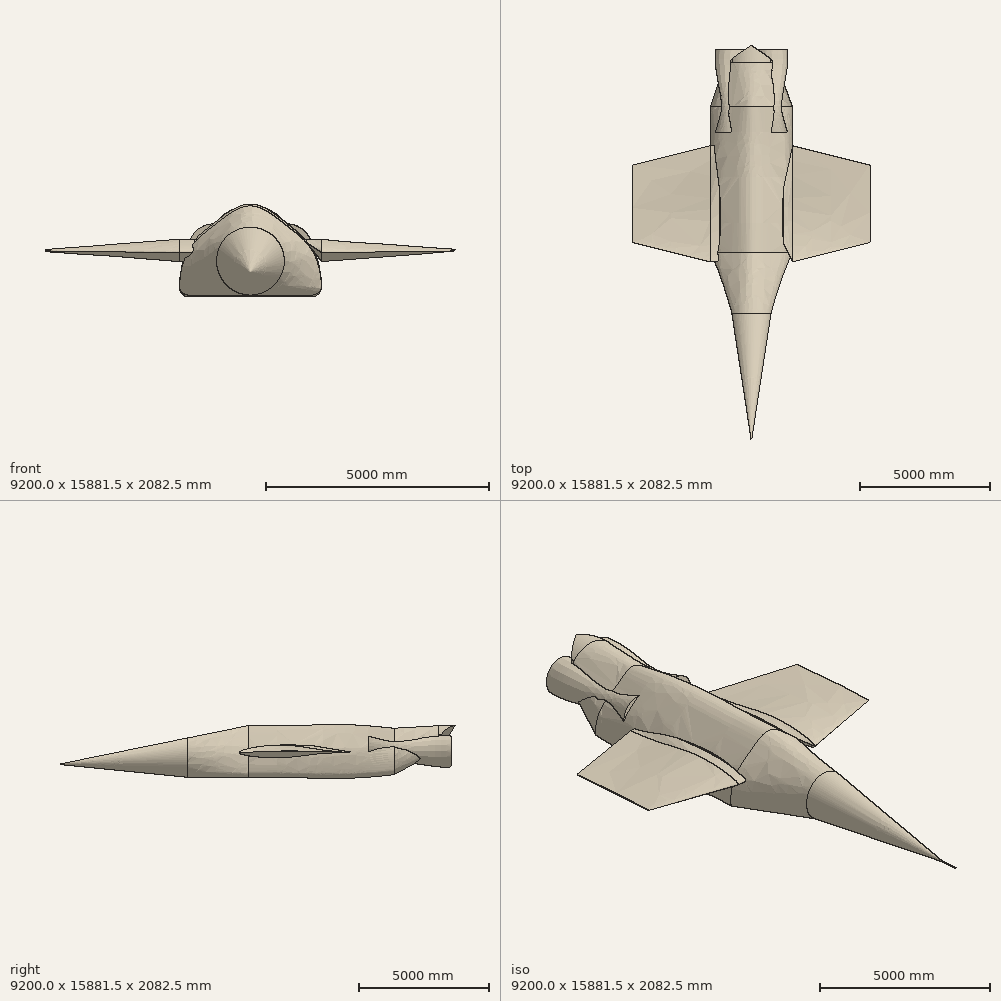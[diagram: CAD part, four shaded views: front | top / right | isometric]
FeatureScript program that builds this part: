
annotation { "Feature Type Name" : "Feature", "Feature Type Description" : "" }
export const myFeature = defineFeature(function(context is Context, id is Id, definition is map)
    precondition{}
    {
        {
            var Q0;
            Q0=qCreatedBy(makeId("Right.planeOp"),FACE);
            var sketch = newSketch(context, id + "F0", { "sketchPlane" : qUnion([Q0])});
            skLineSegment(sketch, "E0", {"start": v(0, 0) * mm, "end": v(-1750, 0) * mm});
            skLineSegment(sketch, "E1", {"start": v(-1750, 0) * mm, "end": v(-3500, 0) * mm});
            skLineSegment(sketch, "E2", {"start": v(-3500, 0) * mm, "end": v(-3500, -1000) * mm});
            skLineSegment(sketch, "E3", {"start": v(-3500, -1000) * mm, "end": v(-8500, -1000) * mm});
            skLineSegment(sketch, "E4", {"start": v(-8500, -1000) * mm, "end": v(-8500, -499.31) * mm});
            skLineSegment(sketch, "E5", {"start": v(-1151.4, 0) * mm, "end": v(-1151.4, 1000) * mm});
            skLineSegment(sketch, "E6", {"start": v(-1151.4, 1000) * mm, "end": v(-8500, -499.31) * mm});
            skLineSegment(sketch, "E7", {"start": v(-8500, -499.31) * mm, "end": v(-3500, -1000) * mm});
            skLineSegment(sketch, "E8", {"start": v(-3500, 0) * mm, "end": v(-3500, 520.82) * mm});
            skLineSegment(sketch, "E9", {"start": v(-8500, -499.31) * mm, "end": v(-8450, -499.31) * mm});
            skLineSegment(sketch, "E10", {"start": v(-8450, -499.31) * mm, "end": v(-8450, -489.1) * mm});
            skLineSegment(sketch, "E11", {"start": v(-8450, -499.31) * mm, "end": v(-8450, -504.32) * mm});
            skSolve(sketch);
        }
        {
            var Q0;
            Q0=sQuery(id+"F0.wireOp",EDGE,"E5");
            cPlane(context, id + "F1", {"entities" : qUnion([Q0]), "cplaneType" : CPlaneType.LINE_ANGLE, "offset" : 25 * mm, "angle" : 90 * degree, "oppositeDirection" : true, "width" : 150 * mm, "height" : 150 * mm});
        }
        {
            var Q0;
            Q0=qCreatedBy(id+"F1.planeOp",FACE);
            var sketch = newSketch(context, id + "F2", { "sketchPlane" : qUnion([Q0])});
            skLineSegment(sketch, "E12.top", {"start": v(-1394.2, -1000) * mm, "end": v(1394.2, -1000) * mm});
            skPoint(sketch, "E12.middle", {"position": v(0, 0) * mm});
            skFitSpline(sketch, "E13", {"points": [v(-1600, -1000) * mm, v(-848, 530) * mm, v(0, 1000) * mm, v(848, 530) * mm, v(1600, -1000) * mm], "startDerivative": vector(0, 10524.75) * mm, "endDerivative": vector(0, -10524.75) * mm});
            skArc(sketch, "E14", {"start": v(-735.27, 618.52) * mm, "mid": v(-1273.27, 435.52) * mm, "end": v(-1440.68, -107.53) * mm});
            skArc(sketch, "E15", {"start": v(1440.68, -107.53) * mm, "mid": v(1273.27, 435.52) * mm, "end": v(735.27, 618.52) * mm});
            skFitSpline(sketch, "E16.trimOffspring", {"points": [v(-1600, -1000) * mm, v(-848, 530) * mm, v(0, 1000) * mm, v(848, 530) * mm, v(1600, -1000) * mm], "startDerivative": vector(0, 10524.75) * mm, "endDerivative": vector(0, -10524.75) * mm});
            skFitSpline(sketch, "E17.trimOffspring", {"points": [v(-1600, -1000) * mm, v(-848, 530) * mm, v(0, 1000) * mm, v(848, 530) * mm, v(1600, -1000) * mm], "startDerivative": vector(0, 10524.75) * mm, "endDerivative": vector(0, -10524.75) * mm});
            skArc(sketch, "E18.filletArc", {"start": v(-1593.82, -787.83) * mm, "mid": v(-1539.85, -937.05) * mm, "end": v(-1394.2, -1000) * mm});
            skArc(sketch, "E19.filletArc", {"start": v(1394.2, -1000) * mm, "mid": v(1539.85, -937.05) * mm, "end": v(1593.82, -787.83) * mm});
            skSolve(sketch);
        }
        {
            var Q0;
            Q0=qCreatedBy(makeId("Front.planeOp"),FACE);
            var sketch = newSketch(context, id + "F3", { "sketchPlane" : qUnion([Q0])});
            skLineSegment(sketch, "E20.top", {"start": v(-1394.2, -1000) * mm, "end": v(1394.2, -1000) * mm});
            skPoint(sketch, "E20.middle", {"position": v(0, 0) * mm});
            skFitSpline(sketch, "E21", {"points": [v(-1600, -1000) * mm, v(-848, 530) * mm, v(0, 1000) * mm, v(848, 530) * mm, v(1600, -1000) * mm], "startDerivative": vector(0, 10524.75) * mm, "endDerivative": vector(0, -10524.75) * mm});
            skArc(sketch, "E22", {"start": v(-735.27, 618.52) * mm, "mid": v(-1273.27, 435.52) * mm, "end": v(-1440.68, -107.53) * mm});
            skArc(sketch, "E23", {"start": v(1440.68, -107.53) * mm, "mid": v(1273.27, 435.52) * mm, "end": v(735.27, 618.52) * mm});
            skFitSpline(sketch, "E24.trimOffspring", {"points": [v(-1600, -1000) * mm, v(-848, 530) * mm, v(0, 1000) * mm, v(848, 530) * mm, v(1600, -1000) * mm], "startDerivative": vector(0, 10524.75) * mm, "endDerivative": vector(0, -10524.75) * mm});
            skFitSpline(sketch, "E25.trimOffspring", {"points": [v(-1600, -1000) * mm, v(-848, 530) * mm, v(0, 1000) * mm, v(848, 530) * mm, v(1600, -1000) * mm], "startDerivative": vector(0, 10524.75) * mm, "endDerivative": vector(0, -10524.75) * mm});
            skArc(sketch, "E26.filletArc", {"start": v(-1593.82, -787.83) * mm, "mid": v(-1539.85, -937.05) * mm, "end": v(-1394.2, -1000) * mm});
            skArc(sketch, "E27.filletArc", {"start": v(1394.2, -1000) * mm, "mid": v(1539.85, -937.05) * mm, "end": v(1593.82, -787.83) * mm});
            skSolve(sketch);
        }
        {
            var Q0;
            Q0=qCreatedBy(makeId("Front.planeOp"),FACE);
            cPlane(context, id + "F4", {"entities" : qUnion([Q0]), "cplaneType" : CPlaneType.OFFSET, "offset" : 3500 * mm, "oppositeDirection" : true, "width" : 150 * mm, "height" : 150 * mm});
        }
        {
            var Q0;
            Q0=qCreatedBy(id+"F4.planeOp",FACE);
            var sketch = newSketch(context, id + "F5", { "sketchPlane" : qUnion([Q0])});
            skLineSegment(sketch, "E28.top", {"start": v(-1394.2, -1000) * mm, "end": v(1394.2, -1000) * mm});
            skPoint(sketch, "E28.middle", {"position": v(0, 0) * mm});
            skFitSpline(sketch, "E29", {"points": [v(-1600, -1000) * mm, v(-848, 530) * mm, v(0, 1000) * mm, v(848, 530) * mm, v(1600, -1000) * mm], "startDerivative": vector(0, 10524.75) * mm, "endDerivative": vector(0, -10524.75) * mm});
            skArc(sketch, "E30", {"start": v(-735.27, 618.52) * mm, "mid": v(-1273.27, 435.52) * mm, "end": v(-1440.68, -107.53) * mm});
            skArc(sketch, "E31", {"start": v(1440.68, -107.53) * mm, "mid": v(1273.27, 435.52) * mm, "end": v(735.27, 618.52) * mm});
            skFitSpline(sketch, "E32.trimOffspring", {"points": [v(-1600, -1000) * mm, v(-848, 530) * mm, v(0, 1000) * mm, v(848, 530) * mm, v(1600, -1000) * mm], "startDerivative": vector(0, 10524.75) * mm, "endDerivative": vector(0, -10524.75) * mm});
            skFitSpline(sketch, "E33.trimOffspring", {"points": [v(-1600, -1000) * mm, v(-848, 530) * mm, v(0, 1000) * mm, v(848, 530) * mm, v(1600, -1000) * mm], "startDerivative": vector(0, 10524.75) * mm, "endDerivative": vector(0, -10524.75) * mm});
            skArc(sketch, "E34.filletArc", {"start": v(-1593.82, -787.83) * mm, "mid": v(-1539.85, -937.05) * mm, "end": v(-1394.2, -1000) * mm});
            skArc(sketch, "E35.filletArc", {"start": v(1394.2, -1000) * mm, "mid": v(1539.85, -937.05) * mm, "end": v(1593.82, -787.83) * mm});
            skSolve(sketch);
        }
        {
            var Q0;
            Q0=qCreatedBy(makeId("Front.planeOp"),FACE);
            cPlane(context, id + "F6", {"entities" : qUnion([Q0]), "cplaneType" : CPlaneType.OFFSET, "offset" : 4500 * mm, "oppositeDirection" : true, "width" : 150 * mm, "height" : 150 * mm});
        }
        {
            var Q0;
            Q0=qCreatedBy(id+"F6.planeOp",FACE);
            var sketch = newSketch(context, id + "F7", { "sketchPlane" : qUnion([Q0])});
            skLineSegment(sketch, "E36.top", {"start": v(-1413.07, -900) * mm, "end": v(1413.07, -900) * mm});
            skPoint(sketch, "E36.middle", {"position": v(0, 0) * mm});
            skFitSpline(sketch, "E37", {"points": [v(-1600, -900) * mm, v(-784.42, 441.24) * mm, v(0, 900) * mm, v(784.42, 441.24) * mm, v(1600, -900) * mm], "startDerivative": vector(0, 9508.62) * mm, "endDerivative": vector(0, -9508.62) * mm});
            skArc(sketch, "E38", {"start": v(-719.25, 488.69) * mm, "mid": v(-1131.76, 394.84) * mm, "end": v(-1324.66, 18.33) * mm});
            skArc(sketch, "E39", {"start": v(1324.66, 18.33) * mm, "mid": v(1131.76, 394.84) * mm, "end": v(719.25, 488.69) * mm});
            skFitSpline(sketch, "E40.trimOffspring", {"points": [v(-1600, -900) * mm, v(-784.42, 441.24) * mm, v(0, 900) * mm, v(784.42, 441.24) * mm, v(1600, -900) * mm], "startDerivative": vector(0, 9508.62) * mm, "endDerivative": vector(0, -9508.62) * mm});
            skFitSpline(sketch, "E41.trimOffspring", {"points": [v(-1600, -900) * mm, v(-784.42, 441.24) * mm, v(0, 900) * mm, v(784.42, 441.24) * mm, v(1600, -900) * mm], "startDerivative": vector(0, 9508.62) * mm, "endDerivative": vector(0, -9508.62) * mm});
            skArc(sketch, "E42.filletArc", {"start": v(-1592.48, -705.43) * mm, "mid": v(-1545.4, -842.02) * mm, "end": v(-1413.07, -900) * mm});
            skArc(sketch, "E43.filletArc", {"start": v(1413.07, -900) * mm, "mid": v(1545.4, -842.02) * mm, "end": v(1592.48, -705.43) * mm});
            skLineSegment(sketch, "E44", {"start": v(-719.25, 488.69) * mm, "end": v(-1324.66, 18.33) * mm, "construction": true});
            skLineSegment(sketch, "E45", {"start": v(719.25, 488.69) * mm, "end": v(1324.66, 18.33) * mm, "construction": true});
            skSolve(sketch);
        }
        {
            var Q0;
            Q0=qCreatedBy(makeId("Front.planeOp"),FACE);
            cPlane(context, id + "F8", {"entities" : qUnion([Q0]), "cplaneType" : CPlaneType.OFFSET, "offset" : 6232.05 * mm, "oppositeDirection" : true, "width" : 150 * mm, "height" : 150 * mm});
        }
        {
            var Q0;
            Q0=qCreatedBy(id+"F8.planeOp",FACE);
            var sketch = newSketch(context, id + "F9", { "sketchPlane" : qUnion([Q0])});
            skArc(sketch, "E46", {"start": v(998.61, 52.63) * mm, "mid": v(0, 1000) * mm, "end": v(-998.61, 52.63) * mm});
            skLineSegment(sketch, "E47", {"start": v(0, 0) * mm, "end": v(-948.68, 0) * mm});
            skLineSegment(sketch, "E48", {"start": v(0, 0) * mm, "end": v(948.68, 0) * mm});
            skLineSegment(sketch, "E49", {"start": v(0, 1000) * mm, "end": v(0, 675) * mm, "construction": true});
            skLineSegment(sketch, "E50", {"start": v(0, 675) * mm, "end": v(-737.82, 675) * mm, "construction": true});
            skLineSegment(sketch, "E51", {"start": v(0, 675) * mm, "end": v(737.82, 675) * mm, "construction": true});
            skPoint(sketch, "E52.visualSharp", {"position": v(-1000, 0) * mm});
            skArc(sketch, "E52.filletArc", {"start": v(-998.61, 52.63) * mm, "mid": v(-984.96, 15.59) * mm, "end": v(-948.68, 0) * mm});
            skPoint(sketch, "E53.visualSharp", {"position": v(1000, 0) * mm});
            skArc(sketch, "E53.filletArc", {"start": v(948.68, 0) * mm, "mid": v(984.96, 15.59) * mm, "end": v(998.61, 52.63) * mm});
            skSolve(sketch);
        }
        {
            var Q0;
            Q0=makeQuery(id+"F2.imprint","IMPRINT",FACE,{"disambiguationData":[TD([[makeQuery(id+"F2.imprint","IMPRINT",EDGE,{"derivedFrom":sQuery(id+"F2.wireOp",EDGE,"E12.top")}),1.0]])]});
            var Q1;
            Q1=makeQuery(id+"F3.imprint","IMPRINT",FACE,{"disambiguationData":[TD([[makeQuery(id+"F3.imprint","IMPRINT",EDGE,{"derivedFrom":sQuery(id+"F3.wireOp",EDGE,"E20.top")}),1.0]])]});
            var Q2;
            Q2=makeQuery(id+"F5.imprint","IMPRINT",FACE,{"disambiguationData":[TD([[makeQuery(id+"F5.imprint","IMPRINT",EDGE,{"derivedFrom":sQuery(id+"F5.wireOp",EDGE,"E28.top")}),1.0]])]});
            var Q3;
            Q3=makeQuery(id+"F7.imprint","IMPRINT",FACE,{"disambiguationData":[TD([[makeQuery(id+"F7.imprint","IMPRINT",EDGE,{"derivedFrom":sQuery(id+"F7.wireOp",EDGE,"E36.top")}),1.0]])]});
            loft(context, id + "F10", {"sheetProfilesArray" : [{ "sheetProfileEntities" : qUnion([Q0]) }, { "sheetProfileEntities" : qUnion([Q1]) }, { "sheetProfileEntities" : qUnion([Q2]) }, { "sheetProfileEntities" : qUnion([Q3]) }]});
        }
        {
            var Q0;
            Q0=sQuery(id+"F7.wireOp",EDGE,"E44");
            var Q1;
            Q1=sQuery(id+"F9.wireOp",VERTEX,"E50.end");
            cPlane(context, id + "F11", {"entities" : qUnion([Q0, Q1]), "cplaneType" : CPlaneType.LINE_ANGLE, "offset" : 25 * mm, "angle" : 180 * degree, "width" : 150 * mm, "height" : 150 * mm});
        }
        {
            var Q0;
            Q0=qCreatedBy(id+"F11.planeOp",FACE);
            var sketch = newSketch(context, id + "F12", { "sketchPlane" : qUnion([Q0])});
            skLineSegment(sketch, "E54", {"start": v(-589.34, 4526.34) * mm, "end": v(-612.8, 6268.32) * mm});
            skLineSegment(sketch, "E55", {"start": v(-1354.08, 4472.19) * mm, "end": v(-612.8, 6268.32) * mm});
            skSolve(sketch);
        }
        {
            var Q0;
            Q0=sQuery(id+"F7.wireOp",EDGE,"E45");
            var Q1;
            Q1=sQuery(id+"F9.wireOp",VERTEX,"E51.end");
            cPlane(context, id + "F13", {"entities" : qUnion([Q0, Q1]), "cplaneType" : CPlaneType.LINE_ANGLE, "offset" : 25 * mm, "angle" : 0 * degree, "width" : 150 * mm, "height" : 150 * mm});
        }
        {
            var Q0;
            Q0=qCreatedBy(id+"F13.planeOp",FACE);
            var sketch = newSketch(context, id + "F14", { "sketchPlane" : qUnion([Q0])});
            skLineSegment(sketch, "E56", {"start": v(589.34, 4526.34) * mm, "end": v(612.8, 6268.32) * mm});
            skLineSegment(sketch, "E57", {"start": v(1354.08, 4472.19) * mm, "end": v(612.8, 6268.32) * mm});
            skSolve(sketch);
        }
        {
            var Q1;
            Q1=makeQuery(id+"F10.opLoft","CAP_FACE",FACE,{"disambiguationData":[OSD([makeQuery(id+"F7.imprint","IMPRINT",FACE,{"disambiguationData":[TD([[makeQuery(id+"F7.imprint","IMPRINT",EDGE,{"derivedFrom":sQuery(id+"F7.wireOp",EDGE,"E36.top")}),1.0]])]})])],"isStart":true});
            var Q2;
            Q2=makeQuery(id+"F9.imprint","IMPRINT",FACE,{"disambiguationData":[TD([[makeQuery(id+"F9.imprint","IMPRINT",EDGE,{"derivedFrom":sQuery(id+"F9.wireOp",EDGE,"E46")}),1.0]])]});
            var Q3;
            Q3=sQuery(id+"F12.wireOp",EDGE,"E54");
            var Q4;
            Q4=sQuery(id+"F14.wireOp",EDGE,"E56");
            loft(context, id + "F15", {"operationType" : NewBodyOperationType.ADD, "addGuides" : true, "sheetProfilesArray" : [{ "sheetProfileEntities" : qUnion([Q1]) }, { "sheetProfileEntities" : qUnion([Q2]) }], "guidesArray" : [{ "guideEntities" : qUnion([Q3]), "guideDerivativeType" : LoftGuideDerivativeType.DEFAULT, "guideDerivativeMagnitude" : 1 }, { "guideEntities" : qUnion([Q4]), "guideDerivativeType" : LoftGuideDerivativeType.DEFAULT, "guideDerivativeMagnitude" : 1 }]});
        }
        {
            var Q0;
            Q0=makeQuery(id+"F15.opLoft","CAP_FACE",FACE,{"disambiguationData":[OSD([makeQuery(id+"F9.imprint","IMPRINT",FACE,{"disambiguationData":[TD([[makeQuery(id+"F9.imprint","IMPRINT",EDGE,{"derivedFrom":sQuery(id+"F9.wireOp",EDGE,"E46")}),1.0]])]})])],"isStart":true});
            extrude(context, id + "F16", {"entities" : qUnion([Q0]), "operationType" : NewBodyOperationType.ADD, "depth" : 649.4 * mm, "offsetDistance" : 25 * mm});
        }
        {
            var Q0;
            Q0=qCreatedBy(makeId("Right.planeOp"),FACE);
            var sketch = newSketch(context, id + "F17", { "sketchPlane" : qUnion([Q0])});
            skLineSegment(sketch, "E58", {"start": v(0, 0) * mm, "end": v(4500, 0) * mm});
            skLineSegment(sketch, "E59", {"start": v(4500, 0) * mm, "end": v(6232.05, 0) * mm});
            skLineSegment(sketch, "E60", {"start": v(4500, 0) * mm, "end": v(4500, 1000) * mm});
            skLineSegment(sketch, "E61", {"start": v(4500, 1000) * mm, "end": v(6881.46, 1000) * mm});
            skLineSegment(sketch, "E62", {"start": v(6881.46, 1000) * mm, "end": v(6881.46, -1000) * mm});
            skLineSegment(sketch, "E63", {"start": v(6881.46, 1000) * mm, "end": v(6232.05, 0) * mm});
            skLineSegment(sketch, "E64", {"start": v(6232.05, 0) * mm, "end": v(5582.64, -1000) * mm});
            skLineSegment(sketch, "E65", {"start": v(5582.64, -1000) * mm, "end": v(6881.46, -1000) * mm});
            skSolve(sketch);
        }
        {
            var Q0;
            Q0=makeQuery(id+"F17.imprint","IMPRINT",FACE,{"disambiguationData":[TD([[makeQuery(id+"F17.imprint","IMPRINT",EDGE,{"derivedFrom":sQuery(id+"F17.wireOp",EDGE,"E62")}),-1.0]])]});
            var Q1;
            Q1=sQuery(id+"F17.wireOp",EDGE,"E61");
            revolve(context, id + "F18", {"operationType" : NewBodyOperationType.REMOVE, "entities" : qUnion([Q0]), "axis" : qUnion([Q1]), "revolveType" : RevolveType.SYMMETRIC, "oppositeDirection" : true, "angle" : 182 * degree});
        }
        {
            var Q0;
            Q0=qCreatedBy(id+"F1.planeOp",FACE);
            var sketch = newSketch(context, id + "F19", { "sketchPlane" : qUnion([Q0])});
            skLineSegment(sketch, "E66.top", {"start": v(-1394.2, -1000) * mm, "end": v(1394.2, -1000) * mm});
            skPoint(sketch, "E66.middle", {"position": v(0, 0) * mm});
            skFitSpline(sketch, "E67", {"points": [v(-1600, -1000) * mm, v(-848, 530) * mm, v(0, 1000) * mm, v(848, 530) * mm, v(1600, -1000) * mm], "startDerivative": vector(0, 10524.75) * mm, "endDerivative": vector(0, -10524.75) * mm});
            skArc(sketch, "E68.filletArc", {"start": v(-1593.82, -787.83) * mm, "mid": v(-1539.85, -937.05) * mm, "end": v(-1394.2, -1000) * mm});
            skArc(sketch, "E69.filletArc", {"start": v(1394.2, -1000) * mm, "mid": v(1539.85, -937.05) * mm, "end": v(1593.82, -787.83) * mm});
            skLineSegment(sketch, "E70", {"start": v(-1593.82, -787.83) * mm, "end": v(-1394.2, -1000) * mm, "construction": true});
            skLineSegment(sketch, "E71", {"start": v(1593.82, -787.83) * mm, "end": v(1394.2, -1000) * mm, "construction": true});
            skSolve(sketch);
        }
        {
            var Q0;
            Q0=qCreatedBy(makeId("Front.planeOp"),FACE);
            cPlane(context, id + "F20", {"entities" : qUnion([Q0]), "cplaneType" : CPlaneType.OFFSET, "offset" : 3500 * mm, "width" : 150 * mm, "height" : 150 * mm});
        }
        {
            var Q0;
            Q0=qCreatedBy(id+"F20.planeOp",FACE);
            var sketch = newSketch(context, id + "F21", { "sketchPlane" : qUnion([Q0])});
            skCircle(sketch, "E72", {"center": v(0, -239.59) * mm, "radius": 760.41 * mm});
            skLineSegment(sketch, "E73", {"start": v(0, -1000) * mm, "end": v(0, -800) * mm, "construction": true});
            skLineSegment(sketch, "E74", {"start": v(0, -800) * mm, "end": v(-513.97, -800) * mm, "construction": true});
            skLineSegment(sketch, "E75", {"start": v(0, -800) * mm, "end": v(513.97, -800) * mm, "construction": true});
            skSolve(sketch);
        }
        {
            var Q0;
            Q0=qCreatedBy(makeId("Front.planeOp"),FACE);
            cPlane(context, id + "F22", {"entities" : qUnion([Q0]), "cplaneType" : CPlaneType.OFFSET, "offset" : 8450 * mm, "width" : 150 * mm, "height" : 150 * mm});
        }
        {
            var Q0;
            Q0=qCreatedBy(id+"F22.planeOp",FACE);
            var sketch = newSketch(context, id + "F23", { "sketchPlane" : qUnion([Q0])});
            skCircle(sketch, "E76", {"center": v(0, -496.71) * mm, "radius": 7.6 * mm});
            skSolve(sketch);
        }
        {
            var Q0;
            Q0=sQuery(id+"F19.wireOp",EDGE,"E70");
            var Q1;
            Q1=sQuery(id+"F21.wireOp",VERTEX,"E74.end");
            cPlane(context, id + "F24", {"entities" : qUnion([Q0, Q1]), "cplaneType" : CPlaneType.LINE_ANGLE, "offset" : 25 * mm, "angle" : 0 * degree, "width" : 150 * mm, "height" : 150 * mm});
        }
        {
            var Q0;
            Q0=qCreatedBy(id+"F24.planeOp",FACE);
            var sketch = newSketch(context, id + "F25", { "sketchPlane" : qUnion([Q0])});
            skLineSegment(sketch, "E77", {"start": v(3032.27, -230.44) * mm, "end": v(558.11, 518.4) * mm});
            skLineSegment(sketch, "E78", {"start": v(3032.27, -230.44) * mm, "end": v(558.11, 227.09) * mm});
            skSolve(sketch);
        }
        {
            var Q0;
            Q0=sQuery(id+"F19.wireOp",EDGE,"E71");
            var Q1;
            Q1=sQuery(id+"F21.wireOp",VERTEX,"E75.end");
            cPlane(context, id + "F26", {"entities" : qUnion([Q0, Q1]), "cplaneType" : CPlaneType.LINE_ANGLE, "offset" : 25 * mm, "angle" : 180 * degree, "width" : 150 * mm, "height" : 150 * mm});
        }
        {
            var Q0;
            Q0=qCreatedBy(id+"F26.planeOp",FACE);
            var sketch = newSketch(context, id + "F27", { "sketchPlane" : qUnion([Q0])});
            skLineSegment(sketch, "E79", {"start": v(-3032.27, -230.44) * mm, "end": v(-558.11, 518.4) * mm});
            skLineSegment(sketch, "E80", {"start": v(-3032.27, -230.44) * mm, "end": v(-558.11, 227.09) * mm});
            skSolve(sketch);
        }
        {
            var Q1;
            Q1=makeQuery(id+"F19.imprint","IMPRINT",FACE,{"disambiguationData":[TD([[makeQuery(id+"F19.imprint","IMPRINT",EDGE,{"derivedFrom":sQuery(id+"F19.wireOp",EDGE,"E66.top")}),1.0]])]});
            var Q2;
            Q2=makeQuery(id+"F21.imprint","IMPRINT",FACE,{"disambiguationData":[TD([[makeQuery(id+"F21.imprint","IMPRINT",EDGE,{"derivedFrom":sQuery(id+"F21.wireOp",EDGE,"E72")}),1.0]])]});
            var Q3;
            Q3=sQuery(id+"F25.wireOp",EDGE,"E77");
            var Q4;
            Q4=sQuery(id+"F27.wireOp",EDGE,"E79");
            loft(context, id + "F28", {"operationType" : NewBodyOperationType.ADD, "addGuides" : true, "sheetProfilesArray" : [{ "sheetProfileEntities" : qUnion([Q1]) }, { "sheetProfileEntities" : qUnion([Q2]) }], "guidesArray" : [{ "guideEntities" : qUnion([Q3]), "guideDerivativeType" : LoftGuideDerivativeType.DEFAULT, "guideDerivativeMagnitude" : 1 }, { "guideEntities" : qUnion([Q4]), "guideDerivativeType" : LoftGuideDerivativeType.DEFAULT, "guideDerivativeMagnitude" : 1 }]});
        }
        {
            var Q1;
            Q1=makeQuery(id+"F28.opLoft","CAP_FACE",FACE,{"disambiguationData":[OSD([makeQuery(id+"F21.imprint","IMPRINT",FACE,{"disambiguationData":[TD([[makeQuery(id+"F21.imprint","IMPRINT",EDGE,{"derivedFrom":sQuery(id+"F21.wireOp",EDGE,"E72")}),1.0]])]})])],"isStart":true});
            var Q2;
            Q2=makeQuery(id+"F23.imprint","IMPRINT",FACE,{"disambiguationData":[TD([[makeQuery(id+"F23.imprint","IMPRINT",EDGE,{"derivedFrom":sQuery(id+"F23.wireOp",EDGE,"E76")}),1.0]])]});
            loft(context, id + "F29", {"operationType" : NewBodyOperationType.ADD, "sheetProfilesArray" : [{ "sheetProfileEntities" : qUnion([Q1]) }, { "sheetProfileEntities" : qUnion([Q2]) }]});
        }
        {
            var Q0;
            Q0=makeQuery(id+"F29.opLoft","CAP_FACE",FACE,{"disambiguationData":[OSD([makeQuery(id+"F23.imprint","IMPRINT",FACE,{"disambiguationData":[TD([[makeQuery(id+"F23.imprint","IMPRINT",EDGE,{"derivedFrom":sQuery(id+"F23.wireOp",EDGE,"E76")}),1.0]])]})])],"isStart":true});
            extrude(context, id + "F30", {"entities" : qUnion([Q0]), "operationType" : NewBodyOperationType.ADD, "depth" : 550 * mm, "offsetDistance" : 25 * mm});
        }
        {
            var Q0;
            Q0=qCreatedBy(makeId("Front.planeOp"),FACE);
            cPlane(context, id + "F31", {"entities" : qUnion([Q0]), "cplaneType" : CPlaneType.OFFSET, "offset" : 3500 * mm, "oppositeDirection" : true, "width" : 150 * mm, "height" : 150 * mm});
        }
        {
            var Q0;
            Q0=qCreatedBy(id+"F31.planeOp",FACE);
            var sketch = newSketch(context, id + "F32", { "sketchPlane" : qUnion([Q0])});
            skCircle(sketch, "E81", {"center": v(-800, 0) * mm, "radius": 600 * mm});
            skCircle(sketch, "E82", {"center": v(800, 0) * mm, "radius": 600 * mm});
            skSolve(sketch);
        }
        {
            var Q0;
            Q0=qCreatedBy(makeId("Front.planeOp"),FACE);
            cPlane(context, id + "F33", {"entities" : qUnion([Q0]), "cplaneType" : CPlaneType.OFFSET, "offset" : 4500 * mm, "oppositeDirection" : true, "width" : 150 * mm, "height" : 150 * mm});
        }
        {
            var Q0;
            Q0=qCreatedBy(id+"F33.planeOp",FACE);
            var sketch = newSketch(context, id + "F34", { "sketchPlane" : qUnion([Q0])});
            skCircle(sketch, "E83", {"center": v(-800, 0) * mm, "radius": 400 * mm});
            skCircle(sketch, "E84", {"center": v(800, 0) * mm, "radius": 400 * mm});
            skSolve(sketch);
        }
        {
            var Q0;
            Q0=qCreatedBy(makeId("Front.planeOp"),FACE);
            cPlane(context, id + "F35", {"entities" : qUnion([Q0]), "cplaneType" : CPlaneType.OFFSET, "offset" : 6232.05 * mm, "oppositeDirection" : true, "width" : 150 * mm, "height" : 150 * mm});
        }
        {
            var Q0;
            Q0=qCreatedBy(id+"F35.planeOp",FACE);
            var sketch = newSketch(context, id + "F36", { "sketchPlane" : qUnion([Q0])});
            skCircle(sketch, "E85", {"center": v(-800, 0) * mm, "radius": 600 * mm});
            skCircle(sketch, "E86", {"center": v(800, 0) * mm, "radius": 600 * mm});
            skSolve(sketch);
        }
        {
            var Q0;
            Q0=qCreatedBy(makeId("Front.planeOp"),FACE);
            cPlane(context, id + "F37", {"entities" : qUnion([Q0]), "cplaneType" : CPlaneType.OFFSET, "offset" : 6732.05 * mm, "oppositeDirection" : true, "width" : 150 * mm, "height" : 150 * mm});
        }
        {
            var Q0;
            Q0=qCreatedBy(id+"F37.planeOp",FACE);
            var sketch = newSketch(context, id + "F38", { "sketchPlane" : qUnion([Q0])});
            skCircle(sketch, "E87", {"center": v(-800, 0) * mm, "radius": 600 * mm});
            skCircle(sketch, "E88", {"center": v(800, 0) * mm, "radius": 600 * mm});
            skSolve(sketch);
        }
        {
            var Q0;
            Q0=makeQuery(id+"F32.imprint","IMPRINT",FACE,{"disambiguationData":[TD([[makeQuery(id+"F32.imprint","IMPRINT",EDGE,{"derivedFrom":sQuery(id+"F32.wireOp",EDGE,"E81")}),1.0]])]});
            var Q1;
            Q1=makeQuery(id+"F34.imprint","IMPRINT",FACE,{"disambiguationData":[TD([[makeQuery(id+"F34.imprint","IMPRINT",EDGE,{"derivedFrom":sQuery(id+"F34.wireOp",EDGE,"E83")}),1.0]])]});
            var Q2;
            Q2=makeQuery(id+"F36.imprint","IMPRINT",FACE,{"disambiguationData":[TD([[makeQuery(id+"F36.imprint","IMPRINT",EDGE,{"derivedFrom":sQuery(id+"F36.wireOp",EDGE,"E85")}),1.0]])]});
            var Q3;
            Q3=makeQuery(id+"F38.imprint","IMPRINT",FACE,{"disambiguationData":[TD([[makeQuery(id+"F38.imprint","IMPRINT",EDGE,{"derivedFrom":sQuery(id+"F38.wireOp",EDGE,"E87")}),1.0]])]});
            loft(context, id + "F39", {"sheetProfilesArray" : [{ "sheetProfileEntities" : qUnion([Q0]) }, { "sheetProfileEntities" : qUnion([Q1]) }, { "sheetProfileEntities" : qUnion([Q2]) }, { "sheetProfileEntities" : qUnion([Q3]) }]});
        }
        {
            var Q0;
            Q0=makeQuery(id+"F32.imprint","IMPRINT",FACE,{"disambiguationData":[TD([[makeQuery(id+"F32.imprint","IMPRINT",EDGE,{"derivedFrom":sQuery(id+"F32.wireOp",EDGE,"E82")}),1.0]])]});
            var Q1;
            Q1=makeQuery(id+"F34.imprint","IMPRINT",FACE,{"disambiguationData":[TD([[makeQuery(id+"F34.imprint","IMPRINT",EDGE,{"derivedFrom":sQuery(id+"F34.wireOp",EDGE,"E84")}),1.0]])]});
            var Q2;
            Q2=makeQuery(id+"F36.imprint","IMPRINT",FACE,{"disambiguationData":[TD([[makeQuery(id+"F36.imprint","IMPRINT",EDGE,{"derivedFrom":sQuery(id+"F36.wireOp",EDGE,"E86")}),1.0]])]});
            var Q3;
            Q3=makeQuery(id+"F38.imprint","IMPRINT",FACE,{"disambiguationData":[TD([[makeQuery(id+"F38.imprint","IMPRINT",EDGE,{"derivedFrom":sQuery(id+"F38.wireOp",EDGE,"E88")}),1.0]])]});
            loft(context, id + "F40", {"sheetProfilesArray" : [{ "sheetProfileEntities" : qUnion([Q0]) }, { "sheetProfileEntities" : qUnion([Q1]) }, { "sheetProfileEntities" : qUnion([Q2]) }, { "sheetProfileEntities" : qUnion([Q3]) }]});
        }
        {
            var Q0;
            Q0=qCreatedBy(makeId("Right.planeOp"),FACE);
            var sketch = newSketch(context, id + "F41", { "sketchPlane" : qUnion([Q0])});
            skFitSpline(sketch, "E89", {"points": [v(-1500, -50) * mm, v(0, 250) * mm, v(3000, -50) * mm, v(0, -250) * mm, v(-1500, -50) * mm]});
            skSolve(sketch);
        }
        {
            var Q0;
            Q0=qCreatedBy(makeId("Right.planeOp"),FACE);
            cPlane(context, id + "F42", {"entities" : qUnion([Q0]), "cplaneType" : CPlaneType.OFFSET, "offset" : 1600 * mm, "oppositeDirection" : true, "width" : 150 * mm, "height" : 150 * mm});
        }
        {
            var Q0;
            Q0=qCreatedBy(id+"F42.planeOp",FACE);
            var sketch = newSketch(context, id + "F43", { "sketchPlane" : qUnion([Q0])});
            skFitSpline(sketch, "E90", {"points": [v(-1500, -50) * mm, v(0, 250) * mm, v(3000, -50) * mm], "startDerivative": vector(0, 887.04) * mm, "endDerivative": vector(7705.35, -256.85) * mm});
            skFitSpline(sketch, "E91", {"points": [v(-1500, -50) * mm, v(0, -250) * mm, v(3000, -50) * mm], "startDerivative": vector(0, -722.87) * mm, "endDerivative": vector(7692.49, -256.42) * mm});
            skSolve(sketch);
        }
        {
            var Q0;
            Q0=qCreatedBy(makeId("Right.planeOp"),FACE);
            cPlane(context, id + "F44", {"entities" : qUnion([Q0]), "cplaneType" : CPlaneType.OFFSET, "offset" : 1600 * mm, "width" : 150 * mm, "height" : 150 * mm});
        }
        {
            var Q0;
            Q0=qCreatedBy(id+"F44.planeOp",FACE);
            var sketch = newSketch(context, id + "F45", { "sketchPlane" : qUnion([Q0])});
            skFitSpline(sketch, "E92", {"points": [v(-1500, -50) * mm, v(0, 250) * mm, v(3000, -50) * mm], "startDerivative": vector(0, 887.04) * mm, "endDerivative": vector(7705.35, -256.85) * mm});
            skFitSpline(sketch, "E93", {"points": [v(-1500, -50) * mm, v(0, -250) * mm, v(3000, -50) * mm], "startDerivative": vector(0, -722.87) * mm, "endDerivative": vector(7692.49, -256.42) * mm});
            skSolve(sketch);
        }
        {
            var Q0;
            Q0=qCreatedBy(makeId("Right.planeOp"),FACE);
            cPlane(context, id + "F46", {"entities" : qUnion([Q0]), "cplaneType" : CPlaneType.OFFSET, "offset" : 4600 * mm, "oppositeDirection" : true, "width" : 150 * mm, "height" : 150 * mm});
        }
        {
            var Q0;
            Q0=qCreatedBy(id+"F46.planeOp",FACE);
            var sketch = newSketch(context, id + "F47", { "sketchPlane" : qUnion([Q0])});
            skFitSpline(sketch, "E94", {"points": [v(-750, -10) * mm, v(250, 25) * mm, v(2250, -10) * mm], "startDerivative": vector(0, 162.94) * mm, "endDerivative": vector(5121.8, -51.22) * mm});
            skFitSpline(sketch, "E95", {"points": [v(-750, -10) * mm, v(750, -25) * mm, v(2250, -10) * mm], "startDerivative": vector(0, -60) * mm, "endDerivative": vector(6000, 0) * mm});
            skSolve(sketch);
        }
        {
            var Q0;
            Q0=qCreatedBy(makeId("Right.planeOp"),FACE);
            cPlane(context, id + "F48", {"entities" : qUnion([Q0]), "cplaneType" : CPlaneType.OFFSET, "offset" : 4600 * mm, "width" : 150 * mm, "height" : 150 * mm});
        }
        {
            var Q0;
            Q0=qCreatedBy(id+"F48.planeOp",FACE);
            var sketch = newSketch(context, id + "F49", { "sketchPlane" : qUnion([Q0])});
            skFitSpline(sketch, "E96", {"points": [v(-750, -10) * mm, v(0, 25) * mm, v(2250, -10) * mm], "startDerivative": vector(1773.58, 123.2) * mm, "endDerivative": vector(4025.46, -103.01) * mm});
            skFitSpline(sketch, "E97", {"points": [v(-750, -10) * mm, v(250, -25) * mm, v(2250, -10) * mm], "startDerivative": vector(2207.02, -49.02) * mm, "endDerivative": vector(3707.2, 43.71) * mm});
            skSolve(sketch);
        }
        {
            var Q0;
            Q0 = qSketchRegion(id + "F41", true);
            extrude(context, id + "F50", {"entities" : qUnion([Q0]), "endBound" : BoundingType.SYMMETRIC, "depth" : 2500 * mm, "offsetDistance" : 25 * mm});
        }
        {
            var Q1;
            Q1=makeQuery(id+"F50.opExtrude","CAP_FACE",FACE,{"disambiguationData":[OSD([sQuery(id+"F41.wireOp",EDGE,"E89")])],"isStart":true});
            var Q2;
            {var subQ0=sQuery(id+"F43.wireOp",EDGE,"E90");Q2=makeQuery(id+"F43.imprint","IMPRINT",FACE,{"disambiguationData":[TD([[makeQuery(id+"F43.imprint","IMPRINT",EDGE,{"derivedFrom":subQ0}),-1.0]])]});}
            loft(context, id + "F51", {"operationType" : NewBodyOperationType.ADD, "sheetProfilesArray" : [{ "sheetProfileEntities" : qUnion([Q1]) }, { "sheetProfileEntities" : qUnion([Q2]) }]});
        }
        {
            var Q1;
            Q1=makeQuery(id+"F50.opExtrude","CAP_FACE",FACE,{"disambiguationData":[OSD([sQuery(id+"F41.wireOp",EDGE,"E89")])],"isStart":false});
            var Q2;
            {var subQ0=sQuery(id+"F45.wireOp",EDGE,"E92");Q2=makeQuery(id+"F45.imprint","IMPRINT",FACE,{"disambiguationData":[TD([[makeQuery(id+"F45.imprint","IMPRINT",EDGE,{"derivedFrom":subQ0}),-1.0]])]});}
            loft(context, id + "F52", {"operationType" : NewBodyOperationType.ADD, "sheetProfilesArray" : [{ "sheetProfileEntities" : qUnion([Q1]) }, { "sheetProfileEntities" : qUnion([Q2]) }]});
        }
        {
            var Q1;
            {var subQ0=sQuery(id+"F43.wireOp",EDGE,"E90");Q1=makeQuery(id+"F51.opLoft","CAP_FACE",FACE,{"disambiguationData":[OSD([makeQuery(id+"F43.imprint","IMPRINT",FACE,{"disambiguationData":[TD([[makeQuery(id+"F43.imprint","IMPRINT",EDGE,{"derivedFrom":subQ0}),-1.0]])]})])],"isStart":true});}
            var Q2;
            Q2=makeQuery(id+"F47.imprint","IMPRINT",FACE,{"disambiguationData":[TD([[makeQuery(id+"F47.imprint","IMPRINT",EDGE,{"derivedFrom":sQuery(id+"F47.wireOp",EDGE,"E94")}),-1.0]])]});
            loft(context, id + "F53", {"operationType" : NewBodyOperationType.ADD, "sheetProfilesArray" : [{ "sheetProfileEntities" : qUnion([Q1]) }, { "sheetProfileEntities" : qUnion([Q2]) }]});
        }
        {
            var Q1;
            {var subQ0=sQuery(id+"F45.wireOp",EDGE,"E92");Q1=makeQuery(id+"F52.opLoft","CAP_FACE",FACE,{"disambiguationData":[OSD([makeQuery(id+"F45.imprint","IMPRINT",FACE,{"disambiguationData":[TD([[makeQuery(id+"F45.imprint","IMPRINT",EDGE,{"derivedFrom":subQ0}),-1.0]])]})])],"isStart":true});}
            var Q2;
            Q2=makeQuery(id+"F49.imprint","IMPRINT",FACE,{"disambiguationData":[TD([[makeQuery(id+"F49.imprint","IMPRINT",EDGE,{"derivedFrom":sQuery(id+"F49.wireOp",EDGE,"E96")}),-1.0]])]});
            loft(context, id + "F54", {"operationType" : NewBodyOperationType.ADD, "sheetProfilesArray" : [{ "sheetProfileEntities" : qUnion([Q1]) }, { "sheetProfileEntities" : qUnion([Q2]) }]});
        }
    });
